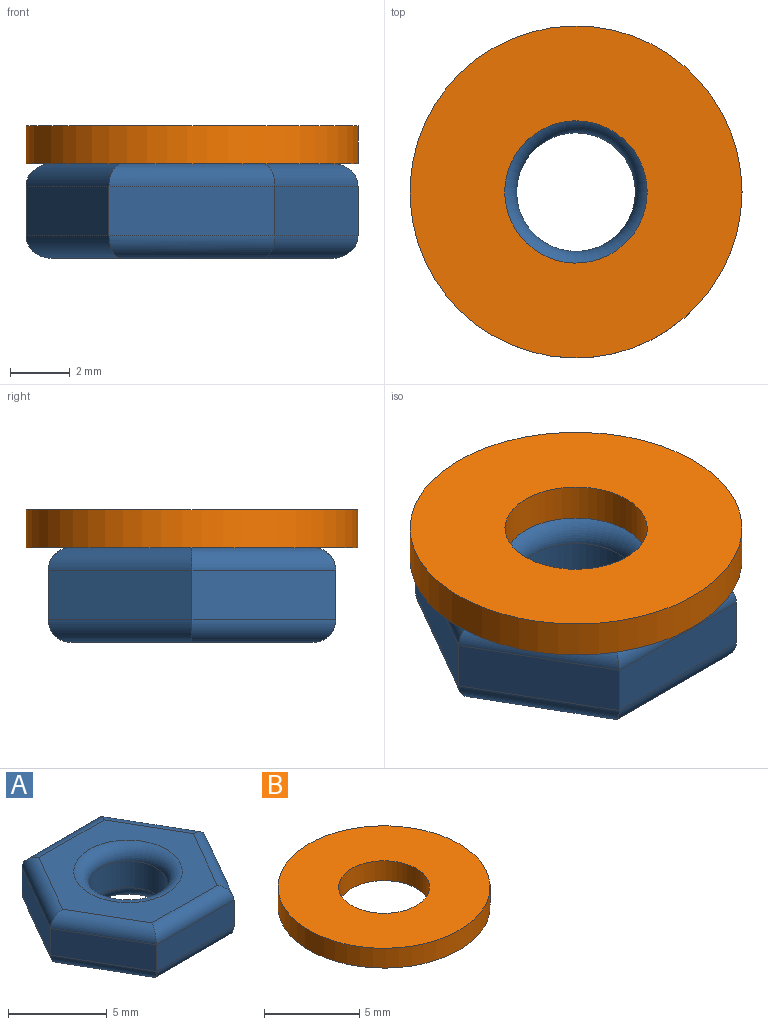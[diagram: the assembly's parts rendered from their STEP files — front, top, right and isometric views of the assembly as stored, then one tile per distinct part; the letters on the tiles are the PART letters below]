
ASSEMBLY  parts=2 mates=1
PART A: 23 faces, bbox 11.1x9.6x3.2 mm
  f0: plane 4.81x2.78mm, normal (0.87,-0.5,0), area 9.2mm2, adj f1,f5,f12,f19
  f1: plane 4.81x2.78mm, normal (0.87,0.5,0), area 9.2mm2, adj f0,f2,f10,f17
  f2: plane 5.56x1.65mm, normal (0,1,0), area 9.2mm2, adj f1,f3,f9,f16
  f3: plane 4.81x2.78mm, normal (-0.87,0.5,0), area 9.2mm2, adj f2,f4,f11,f18
  f4: plane 4.81x2.78mm, normal (-0.87,-0.5,0), area 9.2mm2, adj f3,f5,f13,f20
  f5: plane 5.56x1.65mm, normal (0,-1,0), area 9.2mm2, adj f0,f4,f14,f21
  f6: cylinder r=1.98mm len=3.97mm, axis (0,0,-1), area 20.6mm2, adj f15,f22
  f7: plane 9.35x8.1mm, normal (0,0,1), area 33.1mm2, adj f16,f17,f18,f19,f20,f21,f22
  f8: plane 9.35x8.1mm, normal (0,0,-1), area 33.1mm2, adj f9,f10,f11,f12,f13,f14,f15
  f9: cylinder r=0.76mm len=5.56mm, axis (-1,0,0), area 6.3mm2, adj f2,f8,f10,f11
  f10: cylinder r=0.76mm len=5.19mm, axis (-0.5,0.87,0), area 6.3mm2, adj f1,f8,f9,f12
  f11: cylinder r=0.76mm len=5.19mm, axis (-0.5,-0.87,0), area 6.3mm2, adj f3,f8,f9,f13
  f12: cylinder r=0.76mm len=5.19mm, axis (0.5,0.87,0), area 6.3mm2, adj f0,f8,f10,f14
  f13: cylinder r=0.76mm len=5.19mm, axis (0.5,-0.87,0), area 6.3mm2, adj f4,f8,f11,f14
  f14: cylinder r=0.76mm len=5.56mm, axis (1,0,0), area 6.3mm2, adj f5,f8,f12,f13
  f15: torus R=2.75mm, axis (0,0,1), area 17mm2, adj f6,f8
  f16: cylinder r=0.76mm len=5.56mm, axis (1,0,0), area 6.3mm2, adj f2,f7,f17,f18
  f17: cylinder r=0.76mm len=5.19mm, axis (0.5,-0.87,0), area 6.3mm2, adj f1,f7,f16,f19
  f18: cylinder r=0.76mm len=5.19mm, axis (0.5,0.87,0), area 6.3mm2, adj f3,f7,f16,f20
  f19: cylinder r=0.76mm len=5.19mm, axis (-0.5,-0.87,0), area 6.3mm2, adj f0,f7,f17,f21
  f20: cylinder r=0.76mm len=5.19mm, axis (-0.5,0.87,0), area 6.3mm2, adj f4,f7,f18,f21
  f21: cylinder r=0.76mm len=5.56mm, axis (-1,0,0), area 6.3mm2, adj f5,f7,f19,f20
  f22: torus R=2.75mm, axis (0,0,1), area 17mm2, adj f6,f7
PART B: 4 faces, bbox 11.1x11.1x1.3 mm
  f0: cylinder r=2.38mm len=4.76mm, axis (0,0,-1), area 19mm2, adj f2,f3
  f1: cylinder r=5.56mm len=11.11mm, axis (0,0,-1), area 44.3mm2, adj f2,f3
  f2: plane 11.11x11.11mm, normal (0,0,1), area 79.2mm2, adj f0,f1
  f3: plane 11.11x11.11mm, normal (0,0,-1), area 79.2mm2, adj f0,f1
PLACE A t=(0,0,-1.59)mm
PLACE B t=(0,0,0.64)mm
MATE fastened A.f6 <-> B.f1  axis (0,0,1) through (0,0,0)mm
